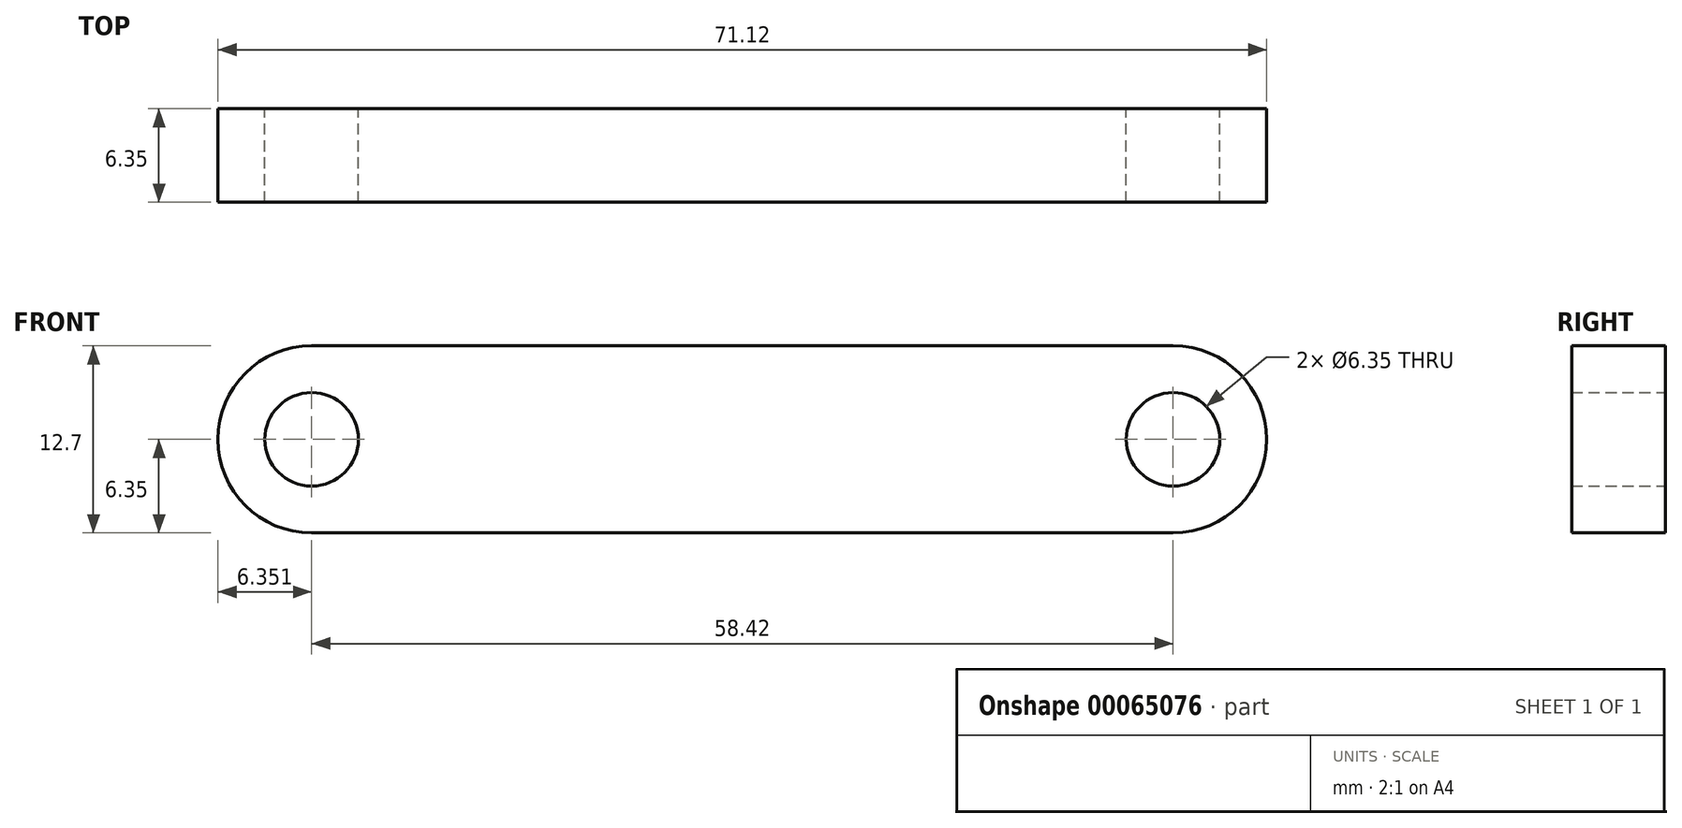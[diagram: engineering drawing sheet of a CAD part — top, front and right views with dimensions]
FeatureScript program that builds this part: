
annotation { "Feature Type Name" : "Feature", "Feature Type Description" : "" }
export const myFeature = defineFeature(function(context is Context, id is Id, definition is map)
    precondition{}
    {
        {
            var Q0;
            Q0=qCreatedBy(makeId("Front.planeOp"),FACE);
            var sketch = newSketch(context, id + "F0", { "sketchPlane" : qUnion([Q0])});
            skLineSegment(sketch, "E0", {"start": v(-78.3, 0) * mm, "end": v(93.51, 0) * mm, "construction": true});
            skLineSegment(sketch, "E1", {"start": v(-28.4, 14.5) * mm, "end": v(-28.4, -17.75) * mm, "construction": true});
            skLineSegment(sketch, "E2", {"start": v(30.02, 15.31) * mm, "end": v(30.02, -22.41) * mm, "construction": true});
            skArc(sketch, "E3", {"start": v(-28.4, 6.35) * mm, "mid": v(-34.75, 0) * mm, "end": v(-28.4, -6.35) * mm});
            skArc(sketch, "E4", {"start": v(30.02, -6.35) * mm, "mid": v(36.37, 0) * mm, "end": v(30.02, 6.35) * mm});
            skCircle(sketch, "E5", {"center": v(-28.4, 0) * mm, "radius": 3.18 * mm});
            skCircle(sketch, "E6", {"center": v(30.02, 0) * mm, "radius": 3.18 * mm});
            skLineSegment(sketch, "E7", {"start": v(-28.4, 6.35) * mm, "end": v(30.02, 6.35) * mm});
            skLineSegment(sketch, "E8", {"start": v(-28.4, -6.35) * mm, "end": v(30.02, -6.35) * mm});
            skSolve(sketch);
        }
        {
            var Q0;
            Q0=makeQuery(id+"F0.imprint","IMPRINT",FACE,{"disambiguationData":[TD([[makeQuery(id+"F0.imprint","IMPRINT",EDGE,{"derivedFrom":sQuery(id+"F0.wireOp",EDGE,"E3")}),1.0]])]});
            extrude(context, id + "F1", {"entities" : qUnion([Q0]), "depth" : 6.35 * mm});
        }
    });
